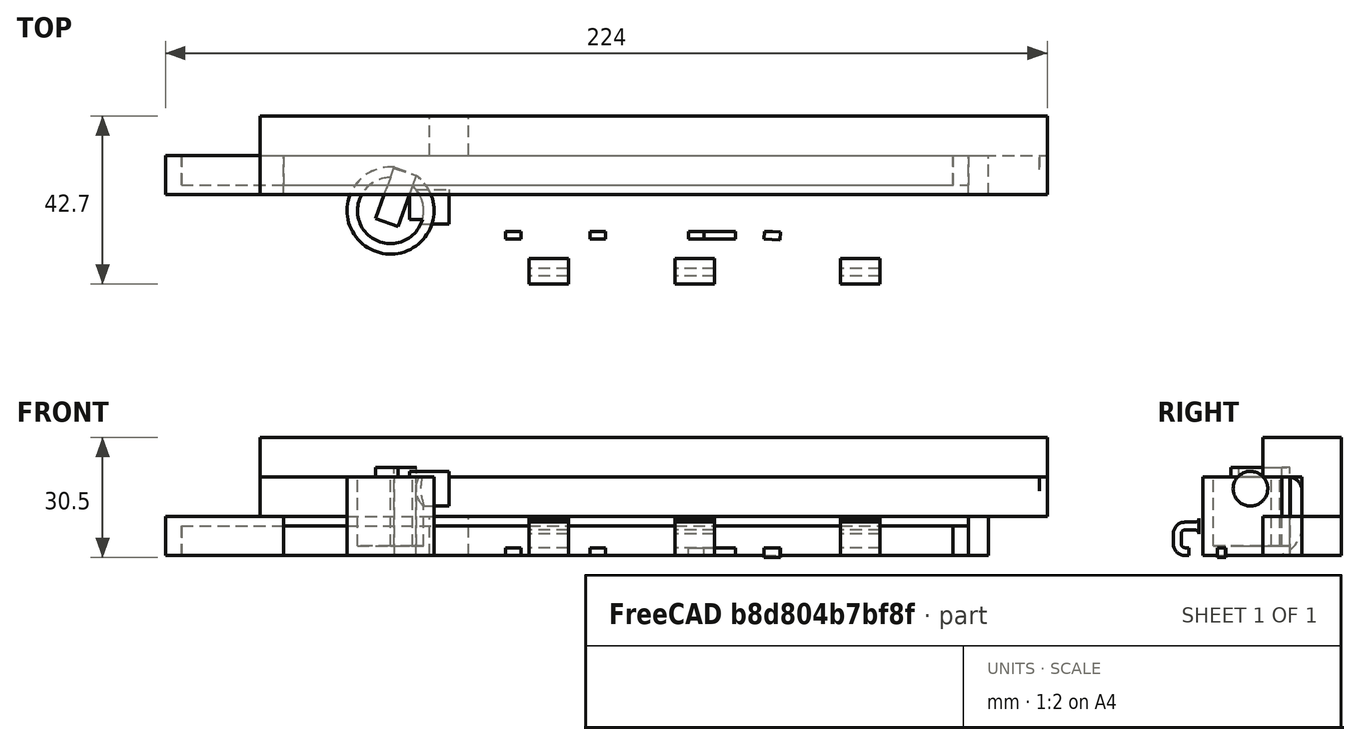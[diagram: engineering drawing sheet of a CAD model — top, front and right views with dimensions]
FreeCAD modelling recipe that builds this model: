
FCSTD DOCUMENT  (FreeCAD 0.19R0.19.2)
Label: v0_72
License: All rights reserved
LicenseURL: http://en.wikipedia.org/wiki/All_rights_reserved
objects: Part::Box×62, Part::Fillet×31, Part::MultiFuse×25, Part::Cut×13, Sketcher::SketchObject×11, Part::Extrusion×9, Part::Cylinder×6, App::MeasureDistance×5, Part::Revolution×1
note: 158 computed .brp shape members not serialized (recipe doc carries the construction recipe); baked Part::Feature solids carry a one-line shape summary decoded from their .brp

FEATURE [Sketcher::SketchObject] Sketch001
  FullyConstrained = true
  sketch-geometry (47):
    g0: Circle CenterX=-129.5 CenterY=-8 CenterZ=0 NormalX=0 NormalY=0 NormalZ=1 AngleXU=0 Radius=1
    g1: Circle CenterX=-129.5 CenterY=-3 CenterZ=0 NormalX=0 NormalY=0 NormalZ=1 AngleXU=0 Radius=1
    g2: Circle CenterX=-124.5 CenterY=-3 CenterZ=0 NormalX=0 NormalY=0 NormalZ=1 AngleXU=0 Radius=1
    g3: BSplineCurve PolesCount=3 KnotsCount=2 Degree=2 IsPeriodic=0
    g4: GeomPoint X=-129.5 Y=-8 Z=0
    g5: GeomPoint X=-124.5 Y=-3 Z=0
    g6: LineSegment StartX=18.6 StartY=-2.9 StartZ=0 EndX=23.6 EndY=-2.9 EndZ=0
    g7: ArcOfCircle CenterX=23.8 CenterY=-14.35 CenterZ=0 NormalX=0 NormalY=0 NormalZ=1 AngleXU=0 Radius=2.3 StartAngle=8e-16 EndAngle=1.5708
    g8: ArcOfCircle CenterX=23.8 CenterY=-18.1 CenterZ=0 NormalX=0 NormalY=0 NormalZ=1 AngleXU=0 Radius=2.3 StartAngle=4.71239 EndAngle=6.28319
    g9: LineSegment StartX=23.8 StartY=-20.4 StartZ=0 EndX=21.1 EndY=-20.4 EndZ=0
    g10: LineSegment StartX=21.1 StartY=-22.9 StartZ=0 EndX=21.1 EndY=-20.4 EndZ=0
    g11: LineSegment StartX=26.1 StartY=-14.35 StartZ=0 EndX=26.1 EndY=-18.1 EndZ=0
    g12: LineSegment StartX=18.6 StartY=-5.40742 StartZ=0 EndX=18.6 EndY=-2.9 EndZ=0
    g13: ArcOfCircle CenterX=18.8 CenterY=-8.1 CenterZ=0 NormalX=0 NormalY=0 NormalZ=1 AngleXU=0 Radius=2.7 StartAngle=1.64494 EndAngle=3.14159
    g14: ArcOfCircle CenterX=18.8 CenterY=-11.85 CenterZ=0 NormalX=0 NormalY=0 NormalZ=1 AngleXU=0 Radius=2.7 StartAngle=3.14159 EndAngle=4.71239
    g15: LineSegment StartX=16.1 StartY=-8.1 StartZ=0 EndX=16.1 EndY=-11.85 EndZ=0
    g16: LineSegment StartX=18.8 StartY=-14.55 StartZ=0 EndX=21.5 EndY=-14.55 EndZ=0
    g17: LineSegment StartX=21.5 StartY=-12.05 StartZ=0 EndX=21.5 EndY=-14.55 EndZ=0
    g18: LineSegment StartX=21.5 StartY=-12.05 StartZ=0 EndX=23.8 EndY=-12.05 EndZ=0
    g19: LineSegment StartX=16.1 StartY=-22.9 StartZ=0 EndX=21.1 EndY=-22.9 EndZ=0
    g20: LineSegment StartX=23.6 StartY=-2.9 StartZ=0 EndX=23.6 EndY=0 EndZ=0
    g21: LineSegment StartX=16.1 StartY=-22.9 StartZ=0 EndX=16.1 EndY=-26.2 EndZ=0
    g22: BSplineCurve PolesCount=3 KnotsCount=2 Degree=2 IsPeriodic=0
    g23: LineSegment StartX=2.6 StartY=-3 StartZ=0 EndX=-124.5 EndY=-3 EndZ=0
    g24: ArcOfCircle CenterX=-134.9 CenterY=-8.6 CenterZ=0 NormalX=0 NormalY=0 NormalZ=1 AngleXU=0 Radius=0.5 StartAngle=4.71238 EndAngle=6.28319
    g25: LineSegment StartX=-141.9 StartY=-9.1 StartZ=0 EndX=-134.9 EndY=-9.1 EndZ=0
    g26: LineSegment StartX=-141.9 StartY=-33.8 StartZ=0 EndX=-141.5 EndY=-33.8 EndZ=0
    g27: LineSegment StartX=-141.9 StartY=-9.1 StartZ=0 EndX=-141.9 EndY=-33.8 EndZ=0
    g28: LineSegment StartX=-134.4 StartY=-8.6 StartZ=0 EndX=-134.4 EndY=0 EndZ=0
    g29: LineSegment StartX=-134.4 StartY=0 StartZ=0 EndX=23.6 EndY=0 EndZ=0
    g30: LineSegment StartX=-133.5 StartY=-26.2 StartZ=0 EndX=16.1 EndY=-26.2 EndZ=0
    g31-g36: Circle x6 (B-spline internal-alignment scaffolding for g37; pole/knot coordinates omitted)
    g37: BSplineCurve PolesCount=6 KnotsCount=4 Degree=3 IsPeriodic=0
    g38-g41: GeomPoint x4 (B-spline internal-alignment scaffolding for g37; pole/knot coordinates omitted)
    g42: BSplineCurve PolesCount=3 KnotsCount=2 Degree=2 IsPeriodic=0
    g43: LineSegment StartX=-129.5 StartY=-8 StartZ=0 EndX=-129.5 EndY=-18.2 EndZ=0
    g44: BSplineCurve PolesCount=3 KnotsCount=2 Degree=2 IsPeriodic=0
    g45: LineSegment StartX=7.6 StartY=-8 StartZ=0 EndX=7.6 EndY=-18.2 EndZ=0
    g46: LineSegment StartX=2.6 StartY=-23.2 StartZ=0 EndX=-124.5 EndY=-23.2 EndZ=0
  constraints (87):
    c: Weight(g0) = 1
    c: Equal(g0,g1)
    c: Equal(g0,g2)
    c: InternalAlignment(g0,g3)
    c: InternalAlignment(g1,g3)
    c: InternalAlignment(g2,g3)
    c: InternalAlignment(g4,g3)
    c: InternalAlignment(g5,g3)
    c: Block(g3)
    c: Block(g8)
    c: Block(g7)
    c: Coincident(g9,g8)
    c: Horizontal(g9)
    c: Vertical(g10)
    c: Coincident(g10,g9)
    c: Coincident(g11,g7)
    c: Coincident(g11,g8)
    c: Vertical(g11)
    c: Vertical(g12)
    c: Block(g12)
    c: Coincident(g6,g12)
    c: Horizontal(g6)
    c: Block(g6)
    c: Coincident(g13,g12)
    c: Block(g14)
    c: Vertical(g15)
    c: Block(g15)
    c: Coincident(g16,g14)
    c: Horizontal(g16)
    c: Vertical(g17)
    c: Coincident(g17,g16)
    c: Block(g17)
    c: Coincident(g18,g7)
    c: Horizontal(g18)
    c: Block(g18)
    c: Coincident(g19,g10)
    c: Horizontal(g19)
    c: Block(g19)
    c: Block(g13)
    c: Coincident(g20,g6)
    c: Vertical(g20)
    c: Vertical(g21)
    c: Block(g21)
    c: Block(g22)
    c: Coincident(g23,g22)
    c: Coincident(g23,g3)
    c: Horizontal(g23)
    c: Block(g24)
    c: Coincident(g25,g24)
    c: Horizontal(g25)
    c: Horizontal(g26)
    c: Block(g26)
    c: Coincident(g27,g25)
    c: Coincident(g27,g26)
    c: Vertical(g27)
    c: Coincident(g28,g24)
    c: Vertical(g28)
    c: Coincident(g29,g28)
    c: Coincident(g29,g20)
    c: Horizontal(g29)
    c: Block(g29)
    c: Block(g25)
    c: Block(g28)
    c: Block(g27)
    c: Coincident(g30,g21)
    c: Horizontal(g30)
    c: Block(g30)
    c: Coincident(g37,g26)
    c: Weight(g31) = 1
    c: Equal(g31, g32-g36) x5
    c: Coincident(g37,g30)
    c: InternalAlignment(g31-g36 -> g37) x6
    c: InternalAlignment(g38-g41 -> g37) x4
    c: Block(g37)
    c: Block(g42)
    c: Coincident(g43,g3)
    c: Coincident(g43,g42)
    c: Vertical(g43)
    c: Distance(g43) = 10.2
    c: Block(g44)
    c: Coincident(g45,g22)
    c: Coincident(g45,g44)
    c: Vertical(g45)
    c: Distance(g45) = 10.2
    c: Coincident(g46,g44)
    c: Coincident(g46,g42)
    c: Horizontal(g46)
FEATURE [Part::Extrusion] Extrude001
  Base = -> Sketch001
  Dir = (0,0,1)
  DirMode = 2
  FaceMakerClass = Part::FaceMakerBullseye
  LengthFwd = 20
  LengthRev = 0
  Solid = true
  Symmetric = false
FEATURE [Sketcher::SketchObject] Sketch004
  FullyConstrained = true
  Placement = pos=(0,0,0) rot=(1,0,0;1.5708rad)
  sketch-geometry (12):
    g0: LineSegment StartX=15.75 StartY=2.5 StartZ=0 EndX=15.75 EndY=0 EndZ=0
    g1: Circle CenterX=15.75 CenterY=2.5 CenterZ=0 NormalX=0 NormalY=0 NormalZ=1 AngleXU=0 Radius=1
    g2: Circle CenterX=10.55 CenterY=2.5 CenterZ=0 NormalX=0 NormalY=0 NormalZ=1 AngleXU=0 Radius=1
    g3: Circle CenterX=10.55 CenterY=8 CenterZ=0 NormalX=0 NormalY=0 NormalZ=1 AngleXU=0 Radius=1
    g4: BSplineCurve PolesCount=3 KnotsCount=2 Degree=2 IsPeriodic=0
    g5: GeomPoint X=15.75 Y=2.5 Z=0
    g6: GeomPoint X=10.55 Y=8 Z=0
    g7: LineSegment StartX=1.9 StartY=8 StartZ=0 EndX=10.55 EndY=8 EndZ=0
    g8: LineSegment StartX=1.9 StartY=-2.4 StartZ=0 EndX=1.9 EndY=8 EndZ=0
    g9: LineSegment StartX=3.30092 StartY=-2.4 StartZ=0 EndX=3.30092 EndY=0 EndZ=0
    g10: LineSegment StartX=15.75 StartY=0 StartZ=0 EndX=3.30092 EndY=0 EndZ=0
    g11: LineSegment StartX=3.30092 StartY=-2.4 StartZ=0 EndX=1.9 EndY=-2.4 EndZ=0
  constraints (26):
    c: Vertical(g0)
    c: Distance(g0) = 2.5
    c: Coincident(g4,g0)
    c: Weight(g1) = 1
    c: Equal(g1,g2)
    c: Equal(g1,g3)
    c: InternalAlignment(g1,g4)
    c: InternalAlignment(g2,g4)
    c: InternalAlignment(g3,g4)
    c: InternalAlignment(g5,g4)
    c: InternalAlignment(g6,g4)
    c: Block(g4)
    c: Coincident(g7,g4)
    c: Horizontal(g7)
    c: Vertical(g8)
    c: Coincident(g8,g7)
    c: Block(g8)
    c: Vertical(g9)
    c: Coincident(g10,g0)
    c: PointOnObject(g10,g-1)
    c: Horizontal(g10)
    c: Coincident(g10,g9)
    c: Block(g9)
    c: Coincident(g11,g9)
    c: Coincident(g11,g8)
    c: Horizontal(g11)
FEATURE [Part::Revolution] Revolve  label="mainScrewStandRevolve"
  Angle = 360
  Axis = (0,0,1)
  Base = (0,0,0)
  FaceMakerClass = Part::FaceMakerBullseye
  Placement = pos=(-101.95,-15.3,0) rot=(0,0,1;0rad)
  Solid = true
  Source = -> Sketch004
  Symmetric = false
FEATURE [Sketcher::SketchObject] Sketch044
  FullyConstrained = true
  MapMode = 4
  Placement = pos=(0,0,0) rot=(0.57735,0.57735,0.57735;2.0944rad)
  sketch-geometry (14):
    g0: LineSegment StartX=6.08745 StartY=-4.11588 StartZ=0 EndX=6.08745 EndY=-2.11589 EndZ=0
    g1: LineSegment StartX=8.08745 StartY=1.38411 StartZ=0 EndX=8.08745 EndY=-1.11589 EndZ=0
    g2: ArcOfCircle CenterX=7.08745 CenterY=-1.11589 CenterZ=0 NormalX=0 NormalY=0 NormalZ=1 AngleXU=0 Radius=1 StartAngle=4.71239 EndAngle=6.28319
    g3: LineSegment StartX=6.08745 StartY=-2.11589 StartZ=0 EndX=7.08745 EndY=-2.11589 EndZ=0
    g4: LineSegment StartX=6.08745 StartY=-4.11588 StartZ=0 EndX=7.08745 EndY=-4.11588 EndZ=0
    g5: ArcOfCircle CenterX=7.08745 CenterY=-1.11589 CenterZ=0 NormalX=0 NormalY=0 NormalZ=1 AngleXU=0 Radius=3 StartAngle=4.71239 EndAngle=6.28319
    g6: ArcOfCircle CenterX=7.08745 CenterY=1.38411 CenterZ=0 NormalX=0 NormalY=0 NormalZ=1 AngleXU=0 Radius=1 StartAngle=5.35e-14 EndAngle=1.5708
    g7: LineSegment StartX=10.0875 StartY=-1.11588 StartZ=0 EndX=10.0875 EndY=1.38411 EndZ=0
    g8: ArcOfCircle CenterX=7.08745 CenterY=1.38411 CenterZ=0 NormalX=0 NormalY=0 NormalZ=1 AngleXU=0 Radius=3 StartAngle=3.57e-14 EndAngle=1.5708
    g9: ArcOfCircle CenterX=4.58745 CenterY=1.38412 CenterZ=0 NormalX=0 NormalY=0 NormalZ=1 AngleXU=0 Radius=1 StartAngle=1.57081 EndAngle=3.14159
    g10: LineSegment StartX=4.58744 StartY=2.38411 StartZ=0 EndX=7.08745 EndY=2.38411 EndZ=0
    g11: LineSegment StartX=4.58745 StartY=4.38411 StartZ=0 EndX=7.08745 EndY=4.38411 EndZ=0
    g12: ArcOfCircle CenterX=4.58745 CenterY=5.38411 CenterZ=0 NormalX=0 NormalY=0 NormalZ=1 AngleXU=0 Radius=1 StartAngle=3.14159 EndAngle=4.71239
    g13: LineSegment StartX=3.58745 StartY=5.38411 StartZ=0 EndX=3.58745 EndY=1.38411 EndZ=0
  constraints (33):
    c: Vertical(g0)
    c: Block(g0)
    c: Block(g1)
    c: Coincident(g2,g1)
    c: Coincident(g3,g0)
    c: Coincident(g3,g2)
    c: Horizontal(g3)
    c: Block(g2)
    c: Coincident(g4,g0)
    c: Horizontal(g4)
    c: Coincident(g5,g2)
    c: Block(g5)
    c: Block(g4)
    c: Coincident(g6,g1)
    c: Block(g6)
    c: Coincident(g7,g5)
    c: Vertical(g7)
    c: Coincident(g8,g6)
    c: Block(g8)
    c: Block(g7)
    c: Coincident(g10,g9)
    c: Coincident(g10,g6)
    c: Horizontal(g10)
    c: Block(g10)
    c: Block(g9)
    c: Coincident(g11,g8)
    c: Horizontal(g11)
    c: Block(g12)
    c: Block(g11)
    c: Coincident(g13,g12)
    c: Coincident(g13,g9)
    c: Vertical(g13)
    c: Tangent(g13,g9)
FEATURE [Sketcher::SketchObject] Sketch045
  FullyConstrained = true
  MapMode = 4
  Placement = pos=(0,0,0) rot=(0.57735,0.57735,0.57735;2.0944rad)
  sketch-geometry (14):
    g0: LineSegment StartX=6.08745 StartY=-4.11588 StartZ=0 EndX=6.08745 EndY=-2.11589 EndZ=0
    g1: LineSegment StartX=8.08745 StartY=1.38411 StartZ=0 EndX=8.08745 EndY=-1.11589 EndZ=0
    g2: ArcOfCircle CenterX=7.08745 CenterY=-1.11589 CenterZ=0 NormalX=0 NormalY=0 NormalZ=1 AngleXU=0 Radius=1 StartAngle=4.71239 EndAngle=6.28319
    g3: LineSegment StartX=6.08745 StartY=-2.11589 StartZ=0 EndX=7.08745 EndY=-2.11589 EndZ=0
    g4: LineSegment StartX=6.08745 StartY=-4.11588 StartZ=0 EndX=7.08745 EndY=-4.11588 EndZ=0
    g5: ArcOfCircle CenterX=7.08745 CenterY=-1.11589 CenterZ=0 NormalX=0 NormalY=0 NormalZ=1 AngleXU=0 Radius=3 StartAngle=4.71239 EndAngle=6.28319
    g6: ArcOfCircle CenterX=7.08745 CenterY=1.38411 CenterZ=0 NormalX=0 NormalY=0 NormalZ=1 AngleXU=0 Radius=1 StartAngle=5.35e-14 EndAngle=1.5708
    g7: LineSegment StartX=10.0875 StartY=-1.11588 StartZ=0 EndX=10.0875 EndY=1.38411 EndZ=0
    g8: ArcOfCircle CenterX=7.08745 CenterY=1.38411 CenterZ=0 NormalX=0 NormalY=0 NormalZ=1 AngleXU=0 Radius=3 StartAngle=3.57e-14 EndAngle=1.5708
    g9: ArcOfCircle CenterX=4.58745 CenterY=1.38412 CenterZ=0 NormalX=0 NormalY=0 NormalZ=1 AngleXU=0 Radius=1 StartAngle=1.57081 EndAngle=3.14159
    g10: LineSegment StartX=4.58744 StartY=2.38411 StartZ=0 EndX=7.08745 EndY=2.38411 EndZ=0
    g11: LineSegment StartX=4.58745 StartY=4.38411 StartZ=0 EndX=7.08745 EndY=4.38411 EndZ=0
    g12: ArcOfCircle CenterX=4.58745 CenterY=5.38411 CenterZ=0 NormalX=0 NormalY=0 NormalZ=1 AngleXU=0 Radius=1 StartAngle=3.14159 EndAngle=4.71239
    g13: LineSegment StartX=3.58745 StartY=5.38411 StartZ=0 EndX=3.58745 EndY=1.38411 EndZ=0
  constraints (33):
    c: Vertical(g0)
    c: Block(g0)
    c: Block(g1)
    c: Coincident(g2,g1)
    c: Coincident(g3,g0)
    c: Coincident(g3,g2)
    c: Horizontal(g3)
    c: Block(g2)
    c: Coincident(g4,g0)
    c: Horizontal(g4)
    c: Coincident(g5,g2)
    c: Block(g5)
    c: Block(g4)
    c: Coincident(g6,g1)
    c: Block(g6)
    c: Coincident(g7,g5)
    c: Vertical(g7)
    c: Coincident(g8,g6)
    c: Block(g8)
    c: Block(g7)
    c: Coincident(g10,g9)
    c: Coincident(g10,g6)
    c: Horizontal(g10)
    c: Block(g10)
    c: Block(g9)
    c: Coincident(g11,g8)
    c: Horizontal(g11)
    c: Block(g12)
    c: Block(g11)
    c: Coincident(g13,g12)
    c: Coincident(g13,g9)
    c: Vertical(g13)
    c: Tangent(g13,g9)
FEATURE [Part::Extrusion] Extrude040
  Base = -> Sketch045
  Dir = (1,0,0)
  DirMode = 2
  FaceMakerClass = Part::FaceMakerBullseye
  LengthFwd = 10
  LengthRev = 0
  Placement = pos=(-71.7,-22.61,4.115) rot=(0,0,1;3.14159rad)
  Solid = true
  Symmetric = false
FEATURE [Part::Box] Box017  label="Cube017"
  AttacherType = Attacher::AttachEngine3D
  Height = 2
  Length = 2
  Placement = pos=(-85.7,-21.3,0) rot=(0,0,1;0rad)
  Width = 2
FEATURE [Part::Box] Box018  label="Cube018"
  AttacherType = Attacher::AttachEngine3D
  Height = 2
  Length = 2
  Placement = pos=(-87.7,-21.3,0) rot=(0,0,1;0rad)
  Width = 2
FEATURE [Part::MultiFuse] Fusion
  Shapes = -> [Box017,Box018]
FEATURE [Part::Box] Box021  label="Cube021"
  AttacherType = Attacher::AttachEngine3D
  Height = 2
  Length = 2
  Placement = pos=(-85.7,-21.3,0) rot=(0,0,1;0rad)
  Width = 2
FEATURE [Part::Box] Box022  label="Cube022"
  AttacherType = Attacher::AttachEngine3D
  Height = 2
  Length = 2
  Placement = pos=(-87.7,-21.3,0) rot=(0,0,1;0rad)
  Width = 2
FEATURE [Part::Box] Box023  label="Cube023"
  AttacherType = Attacher::AttachEngine3D
  Height = 2
  Length = 2
  Placement = pos=(-85.7,-21.3,0) rot=(0,0,1;0rad)
  Width = 2
FEATURE [Part::Box] Box024  label="Cube024"
  AttacherType = Attacher::AttachEngine3D
  Height = 2
  Length = 2
  Placement = pos=(-87.7,-21.3,0) rot=(0,0,1;0rad)
  Width = 2
FEATURE [Part::Box] Box026  label="Cube026"
  AttacherType = Attacher::AttachEngine3D
  Height = 2
  Length = 2
  Placement = pos=(-87.7,-21.3,0) rot=(0,0,1;0rad)
  Width = 2
FEATURE [Part::Box] Box  label="Cube"
  AttacherType = Attacher::AttachEngine3D
  Height = 10
  Length = 10
  Placement = pos=(-107,0,0) rot=(0,0,1;0rad)
  Width = 10
FEATURE [Sketcher::SketchObject] Sketch046
  FullyConstrained = true
  MapMode = 4
  Placement = pos=(0,0,0) rot=(0.57735,0.57735,0.57735;2.0944rad)
  sketch-geometry (14):
    g0: LineSegment StartX=6.08745 StartY=-4.11588 StartZ=0 EndX=6.08745 EndY=-2.11589 EndZ=0
    g1: LineSegment StartX=8.08745 StartY=1.38411 StartZ=0 EndX=8.08745 EndY=-1.11589 EndZ=0
    g2: ArcOfCircle CenterX=7.08745 CenterY=-1.11589 CenterZ=0 NormalX=0 NormalY=0 NormalZ=1 AngleXU=0 Radius=1 StartAngle=4.71239 EndAngle=6.28319
    g3: LineSegment StartX=6.08745 StartY=-2.11589 StartZ=0 EndX=7.08745 EndY=-2.11589 EndZ=0
    g4: LineSegment StartX=6.08745 StartY=-4.11588 StartZ=0 EndX=7.08745 EndY=-4.11588 EndZ=0
    g5: ArcOfCircle CenterX=7.08745 CenterY=-1.11589 CenterZ=0 NormalX=0 NormalY=0 NormalZ=1 AngleXU=0 Radius=3 StartAngle=4.71239 EndAngle=6.28319
    g6: ArcOfCircle CenterX=7.08745 CenterY=1.38411 CenterZ=0 NormalX=0 NormalY=0 NormalZ=1 AngleXU=0 Radius=1 StartAngle=5.35e-14 EndAngle=1.5708
    g7: LineSegment StartX=10.0875 StartY=-1.11588 StartZ=0 EndX=10.0875 EndY=1.38411 EndZ=0
    g8: ArcOfCircle CenterX=7.08745 CenterY=1.38411 CenterZ=0 NormalX=0 NormalY=0 NormalZ=1 AngleXU=0 Radius=3 StartAngle=3.57e-14 EndAngle=1.5708
    g9: ArcOfCircle CenterX=4.58745 CenterY=1.38412 CenterZ=0 NormalX=0 NormalY=0 NormalZ=1 AngleXU=0 Radius=1 StartAngle=1.57081 EndAngle=3.14159
    g10: LineSegment StartX=4.58744 StartY=2.38411 StartZ=0 EndX=7.08745 EndY=2.38411 EndZ=0
    g11: LineSegment StartX=4.58745 StartY=4.38411 StartZ=0 EndX=7.08745 EndY=4.38411 EndZ=0
    g12: ArcOfCircle CenterX=4.58745 CenterY=5.38411 CenterZ=0 NormalX=0 NormalY=0 NormalZ=1 AngleXU=0 Radius=1 StartAngle=3.14159 EndAngle=4.71239
    g13: LineSegment StartX=3.58745 StartY=5.38411 StartZ=0 EndX=3.58745 EndY=1.38411 EndZ=0
  constraints (33):
    c: Vertical(g0)
    c: Block(g0)
    c: Block(g1)
    c: Coincident(g2,g1)
    c: Coincident(g3,g0)
    c: Coincident(g3,g2)
    c: Horizontal(g3)
    c: Block(g2)
    c: Coincident(g4,g0)
    c: Horizontal(g4)
    c: Coincident(g5,g2)
    c: Block(g5)
    c: Block(g4)
    c: Coincident(g6,g1)
    c: Block(g6)
    c: Coincident(g7,g5)
    c: Vertical(g7)
    c: Coincident(g8,g6)
    c: Block(g8)
    c: Block(g7)
    c: Coincident(g10,g9)
    c: Coincident(g10,g6)
    c: Horizontal(g10)
    c: Block(g10)
    c: Block(g9)
    c: Coincident(g11,g8)
    c: Horizontal(g11)
    c: Block(g12)
    c: Block(g11)
    c: Coincident(g13,g12)
    c: Coincident(g13,g9)
    c: Vertical(g13)
    c: Tangent(g13,g9)
FEATURE [Part::Extrusion] Extrude041
  Base = -> Sketch046
  Dir = (1,0,0)
  DirMode = 2
  FaceMakerClass = Part::FaceMakerBullseye
  LengthFwd = 10
  LengthRev = 0
  Placement = pos=(7.5,-22.61,4.115) rot=(0,0,1;3.14159rad)
  Solid = true
  Symmetric = false
FEATURE [Part::Box] Box027  label="Cube027"
  AttacherType = Attacher::AttachEngine3D
  Height = 2
  Length = 2
  Placement = pos=(-85.7,-21.3,0) rot=(0,0,1;0rad)
  Width = 2
FEATURE [Part::Box] Box028  label="Cube028"
  AttacherType = Attacher::AttachEngine3D
  Height = 2
  Length = 2
  Placement = pos=(-87.7,-21.3,0) rot=(0,0,1;0rad)
  Width = 2
FEATURE [Part::MultiFuse] Fusion009
  Placement = pos=(21.5,0,0) rot=(0,0,1;0rad)
  Shapes = -> [Box027,Box028]
FEATURE [Part::Box] Box029  label="Cube029"
  AttacherType = Attacher::AttachEngine3D
  Height = 2
  Length = 2
  Placement = pos=(-87.7,-21.3,0) rot=(0,0,1;0rad)
  Width = 2
FEATURE [Part::Box] Box030  label="Cube030"
  AttacherType = Attacher::AttachEngine3D
  Height = 2
  Length = 2
  Placement = pos=(-85.7,-21.3,0) rot=(0,0,1;0rad)
  Width = 2
FEATURE [Part::MultiFuse] Fusion010
  Shapes = -> [Box030,Box029]
FEATURE [Part::Box] Box032  label="Cube032"
  AttacherType = Attacher::AttachEngine3D
  Height = 2
  Length = 2
  Placement = pos=(-85.7,-21.3,0) rot=(0,0,1;0rad)
  Width = 2
FEATURE [Part::Box] Box033  label="Cube033"
  AttacherType = Attacher::AttachEngine3D
  Height = 2
  Length = 2
  Placement = pos=(-87.7,-21.3,0) rot=(0,0,1;0rad)
  Width = 2
FEATURE [Part::MultiFuse] Fusion011
  Shapes = -> [Box032,Box033]
FEATURE [Part::Box] Box034  label="Cube034"
  AttacherType = Attacher::AttachEngine3D
  Height = 2
  Length = 2
  Placement = pos=(-85.7,-21.3,0) rot=(0,0,1;0rad)
  Width = 2
FEATURE [Part::Box] Box035  label="Cube035"
  AttacherType = Attacher::AttachEngine3D
  Height = 2
  Length = 2
  Placement = pos=(-87.7,-21.3,0) rot=(0,0,1;0rad)
  Width = 2
FEATURE [Part::Box] Box036  label="Cube036"
  AttacherType = Attacher::AttachEngine3D
  Height = 2
  Length = 2
  Placement = pos=(-85.7,-21.3,0) rot=(0,0,1;0rad)
  Width = 2
FEATURE [Part::Box] Box037  label="Cube037"
  AttacherType = Attacher::AttachEngine3D
  Height = 2
  Length = 2
  Placement = pos=(-87.7,-21.3,0) rot=(0,0,1;0rad)
  Width = 2
FEATURE [Part::Box] Box038  label="Cube038"
  AttacherType = Attacher::AttachEngine3D
  Height = 2
  Length = 2
  Placement = pos=(-85.7,-21.3,0) rot=(0,0,1;0rad)
  Width = 2
FEATURE [Part::Box] Box039  label="Cube039"
  AttacherType = Attacher::AttachEngine3D
  Height = 2
  Length = 2
  Placement = pos=(-87.7,-21.3,0) rot=(0,0,1;0rad)
  Width = 2
FEATURE [Part::Box] Box040  label="Cube040"
  AttacherType = Attacher::AttachEngine3D
  Height = 2
  Length = 2
  Placement = pos=(-85.7,-21.3,0) rot=(0,0,1;0rad)
  Width = 2
FEATURE [Part::Box] Box041  label="Cube041"
  AttacherType = Attacher::AttachEngine3D
  Height = 2
  Length = 2
  Placement = pos=(-87.7,-21.3,0) rot=(0,0,1;0rad)
  Width = 2
FEATURE [Part::Box] Box042  label="Cube042"
  AttacherType = Attacher::AttachEngine3D
  Height = 2
  Length = 2
  Placement = pos=(-87.7,-21.3,0) rot=(0,0,1;0rad)
  Width = 2
FEATURE [Part::Box] Box043  label="Cube043"
  AttacherType = Attacher::AttachEngine3D
  Height = 2
  Length = 2
  Placement = pos=(-85.7,-21.3,0) rot=(0,0,1;0rad)
  Width = 2
FEATURE [Part::MultiFuse] Fusion019
  Placement = pos=(46.5,0,0) rot=(0,0,1;0rad)
  Shapes = -> [Box043,Box042]
FEATURE [Part::Box] Box044  label="Cube044"
  AttacherType = Attacher::AttachEngine3D
  Height = 2
  Length = 2
  Placement = pos=(-87.7,-21.3,0) rot=(0,0,1;0rad)
  Width = 2
FEATURE [Part::Box] Box045  label="Cube045"
  AttacherType = Attacher::AttachEngine3D
  Height = 2
  Length = 2
  Placement = pos=(-85.7,-21.3,0) rot=(0,0,1;0rad)
  Width = 2
FEATURE [Part::MultiFuse] Fusion020
  Placement = pos=(69.3,0,0) rot=(0,0,1;0rad)
  Shapes = -> [Box045,Box044]
FEATURE [Part::Box] Box046  label="Cube046"
  AttacherType = Attacher::AttachEngine3D
  Height = 2
  Length = 2
  Placement = pos=(-87.7,-21.3,0) rot=(0,0,1;0rad)
  Width = 2
FEATURE [Part::Box] Box047  label="Cube047"
  AttacherType = Attacher::AttachEngine3D
  Height = 2
  Length = 2
  Placement = pos=(-85.7,-21.3,0) rot=(0,0,1;0rad)
  Width = 2
FEATURE [Part::MultiFuse] Fusion021
  Placement = pos=(73.3,0,0) rot=(0,0,1;0rad)
  Shapes = -> [Box047,Box046]
FEATURE [Part::Box] Box048  label="Cube048"
  AttacherType = Attacher::AttachEngine3D
  Height = 2
  Length = 2
  Placement = pos=(-87.7,-21.3,0) rot=(0,0,1;0rad)
  Width = 2
FEATURE [Part::Box] Box049  label="Cube049"
  AttacherType = Attacher::AttachEngine3D
  Height = 2
  Length = 2
  Placement = pos=(-85.7,-21.3,0) rot=(0,0,1;0rad)
  Width = 2
FEATURE [Part::MultiFuse] Fusion022
  Placement = pos=(64.3,0,0) rot=(0,0,1;0rad)
  Shapes = -> [Box049,Box048]
FEATURE [Part::MultiFuse] Fusion024
  Shapes = -> [Box034,Box035,Box036,Box037,Box038,Box039,Box040,Box041]
FEATURE [Part::MultiFuse] Fusion025
  Shapes = -> [Box021,Box022,Box023,Box024,Box026]
FEATURE [Part::Box] Box005  label="Cube005"
  AttacherType = Attacher::AttachEngine3D
  Height = 10
  Length = 198
  Placement = pos=(-30,0,0) rot=(0,0,1;0rad)
  Width = 10
FEATURE [Part::Box] Box004  label="Cube004"
  AttacherType = Attacher::AttachEngine3D
  Height = 10
  Length = 200
  Placement = pos=(-30,0,0) rot=(0,0,1;0rad)
  Width = 10
FEATURE [Part::Fillet] Fillet020
  Base = -> Box004
  Edges = 1 edges r=3.6: [Edge12]
FEATURE [Sketcher::SketchObject] Sketch
  FullyConstrained = true
  sketch-geometry (35):
    g0: Circle CenterX=-101.95 CenterY=-14.3 CenterZ=0 NormalX=0 NormalY=0 NormalZ=1 AngleXU=0 Radius=3.25
    g1: LineSegment StartX=16.1 StartY=-26.2 StartZ=0 EndX=16.1 EndY=-22.9 EndZ=0
    g2: ArcOfCircle CenterX=23.8 CenterY=-14.35 CenterZ=0 NormalX=0 NormalY=0 NormalZ=1 AngleXU=0 Radius=2.3 StartAngle=8e-16 EndAngle=1.5708
    g3: LineSegment StartX=18.6 StartY=-5.40742 StartZ=0 EndX=18.6 EndY=-2.9 EndZ=0
    g4: LineSegment StartX=18.6 StartY=-2.9 StartZ=0 EndX=23.6 EndY=-2.9 EndZ=0
    g5: LineSegment StartX=23.6 StartY=-2.9 StartZ=0 EndX=23.6 EndY=2.58e-14 EndZ=0
    g6: LineSegment StartX=18.8 StartY=-14.55 StartZ=0 EndX=21.5 EndY=-14.55 EndZ=0
    g7: LineSegment StartX=21.5 StartY=-12.05 StartZ=0 EndX=21.5 EndY=-14.55 EndZ=0
    g8: LineSegment StartX=21.5 StartY=-12.05 StartZ=0 EndX=23.8 EndY=-12.05 EndZ=0
    g9: ArcOfCircle CenterX=23.8 CenterY=-18.1 CenterZ=0 NormalX=0 NormalY=0 NormalZ=1 AngleXU=0 Radius=2.3 StartAngle=4.71239 EndAngle=6.28319
    g10: LineSegment StartX=23.8 StartY=-20.4 StartZ=0 EndX=21.1 EndY=-20.4 EndZ=0
    g11: LineSegment StartX=26.1 StartY=-14.35 StartZ=0 EndX=26.1 EndY=-18.1 EndZ=0
    g12: ArcOfCircle CenterX=18.8 CenterY=-8.1 CenterZ=0 NormalX=0 NormalY=0 NormalZ=1 AngleXU=0 Radius=2.7 StartAngle=1.64494 EndAngle=3.14159
    g13: ArcOfCircle CenterX=18.8 CenterY=-11.85 CenterZ=0 NormalX=0 NormalY=0 NormalZ=1 AngleXU=0 Radius=2.7 StartAngle=3.14159 EndAngle=4.71239
    g14: LineSegment StartX=16.1 StartY=-8.1 StartZ=0 EndX=16.1 EndY=-11.85 EndZ=0
    g15: LineSegment StartX=21.1 StartY=-22.9 StartZ=0 EndX=21.1 EndY=-20.4 EndZ=0
    g16: LineSegment StartX=16.1 StartY=-22.9 StartZ=0 EndX=21.1 EndY=-22.9 EndZ=0
    g17: LineSegment StartX=23.6 StartY=2.58e-14 StartZ=0 EndX=-134.4 EndY=2.58e-14 EndZ=0
    g18: LineSegment StartX=-134.4 StartY=2.59e-14 StartZ=0 EndX=-134.4 EndY=-8.6 EndZ=0
    g19: ArcOfCircle CenterX=-134.9 CenterY=-8.6 CenterZ=0 NormalX=0 NormalY=0 NormalZ=1 AngleXU=0 Radius=0.5 StartAngle=4.71238 EndAngle=6.28319
    g20: LineSegment StartX=-134.9 StartY=-9.1 StartZ=0 EndX=-141.9 EndY=-9.1 EndZ=0
    g21: LineSegment StartX=-141.9 StartY=-9.1 StartZ=0 EndX=-141.9 EndY=-33.8 EndZ=0
    g22: LineSegment StartX=-141.9 StartY=-33.8 StartZ=0 EndX=-141.5 EndY=-33.8 EndZ=0
    g23: LineSegment StartX=-133.5 StartY=-26.2 StartZ=0 EndX=16.1 EndY=-26.2 EndZ=0
    g24-g29: Circle x6 (B-spline internal-alignment scaffolding for g30; pole/knot coordinates omitted)
    g30: BSplineCurve PolesCount=6 KnotsCount=4 Degree=3 IsPeriodic=0
    g31-g34: GeomPoint x4 (B-spline internal-alignment scaffolding for g30; pole/knot coordinates omitted)
  constraints (61):
    c: Block(g0)
    c: Vertical(g1)
    c: Distance(g1) = 3.3
    c: Block(g9)
    c: Block(g2)
    c: Coincident(g10,g9)
    c: Horizontal(g10)
    c: Vertical(g15)
    c: Coincident(g15,g10)
    c: Coincident(g11,g2)
    c: Coincident(g11,g9)
    c: Vertical(g11)
    c: Vertical(g3)
    c: Block(g3)
    c: Coincident(g4,g3)
    c: Horizontal(g4)
    c: Vertical(g5)
    c: Block(g5)
    c: Block(g4)
    c: Coincident(g12,g3)
    c: Block(g13)
    c: Coincident(g14,g12)
    c: Vertical(g14)
    c: Block(g14)
    c: Coincident(g6,g13)
    c: Horizontal(g6)
    c: Vertical(g7)
    c: Coincident(g7,g6)
    c: Block(g7)
    c: Coincident(g8,g2)
    c: Horizontal(g8)
    c: Block(g8)
    c: Coincident(g16,g15)
    c: Horizontal(g16)
    c: Block(g16)
    c: Block(g12)
    c: Coincident(g16,g1)
    c: Coincident(g17,g5)
    c: Horizontal(g17)
    c: Vertical(g18)
    c: Horizontal(g20)
    c: Coincident(g19,g18)
    c: Coincident(g19,g20)
    c: Block(g19)
    c: Coincident(g21,g20)
    c: Vertical(g21)
    c: Block(g21)
    c: Coincident(g22,g21)
    c: Horizontal(g22)
    c: Block(g22)
    c: Block(g18)
    c: Coincident(g18,g17)
    c: Coincident(g23,g1)
    c: Horizontal(g23)
    c: Distance(g23) = 149.6
    c: Coincident(g30,g22)
    c: Weight(g24) = 1
    c: Equal(g24, g25-g29) x5
    c: InternalAlignment(g24-g29 -> g30) x6
    c: InternalAlignment(g31-g34 -> g30) x4
    c: Block(g30)
FEATURE [Part::Extrusion] Extrude
  Base = -> Sketch
  Dir = (0,0,1)
  DirMode = 2
  FaceMakerClass = Part::FaceMakerBullseye
  LengthFwd = 2.4
  LengthRev = 0
  Solid = true
  Symmetric = false
FEATURE [Part::Box] Box051  label="Cube051"
  AttacherType = Attacher::AttachEngine3D
  Height = 10
  Length = 198
  Placement = pos=(-30,0,0) rot=(0,0,1;0rad)
  Width = 10
FEATURE [Part::Box] Box052  label="Cube052"
  AttacherType = Attacher::AttachEngine3D
  Height = 5
  Length = 200
  Placement = pos=(-30,6.4,10) rot=(1,0,0;0rad)
  Width = 5
FEATURE [Part::Box] Box053  label="Cube053"
  AttacherType = Attacher::AttachEngine3D
  Height = 5
  Length = 200
  Placement = pos=(-30,6.4,10) rot=(1,0,0;0.872665rad)
  Width = 5
FEATURE [Part::Box] Box054  label="Cube054"
  AttacherType = Attacher::AttachEngine3D
  Height = 10
  Length = 200
  Placement = pos=(-30,0,0) rot=(0,0,1;0rad)
  Width = 10
FEATURE [Part::Fillet] Fillet021
  Base = -> Box054
  Edges = 1 edges r=3.6: [Edge12]
FEATURE [Part::Cut] Cut015
  Base = -> Box051
  Tool = -> Fillet021
FEATURE [Part::MultiFuse] Fusion033  label="removeFromMainFusion014"
  Placement = pos=(-120,-10,10) rot=(0,0,1;0rad)
  Shapes = -> [Box053,Box052,Cut015]
FEATURE [Part::Box] Box055  label="Cube055"
  AttacherType = Attacher::AttachEngine3D
  Height = 10
  Length = 190
  Placement = pos=(-30,0,0) rot=(0,0,1;0rad)
  Width = 10
FEATURE [Part::Box] Box056  label="Cube056"
  AttacherType = Attacher::AttachEngine3D
  Height = 10
  Length = 190
  Placement = pos=(-35,0,0) rot=(0,0,1;0rad)
  Width = 10
FEATURE [Part::Fillet] Fillet022
  Base = -> Box055
  Edges = 1 edges r=7.5: [Edge11]
FEATURE [Part::Cut] Cut014  label="filletMain001"
  Base = -> Box056
  Placement = pos=(-120,-10,0) rot=(0,0,1;0rad)
  Tool = -> Fillet022
FEATURE [Part::MultiFuse] Fusion032  label="removeFromMain001"
  Shapes = -> [Fusion033,Cut014]
FEATURE [Part::Cut] Cut017
  Base = -> Extrude
  Tool = -> Fusion032
FEATURE [Part::Box] Box063  label="Cube063"
  AttacherType = Attacher::AttachEngine3D
  Height = 10
  Length = 198
  Placement = pos=(-30,0,0) rot=(0,0,1;0rad)
  Width = 10
FEATURE [Part::Box] Box064  label="Cube064"
  AttacherType = Attacher::AttachEngine3D
  Height = 5
  Length = 200
  Placement = pos=(-30,6.4,10) rot=(1,0,0;0rad)
  Width = 5
FEATURE [Part::Box] Box065  label="Cube065"
  AttacherType = Attacher::AttachEngine3D
  Height = 5
  Length = 200
  Placement = pos=(-30,6.4,10) rot=(1,0,0;0.872665rad)
  Width = 5
FEATURE [Part::Box] Box066  label="Cube066"
  AttacherType = Attacher::AttachEngine3D
  Height = 10
  Length = 200
  Placement = pos=(-30,0,0) rot=(0,0,1;0rad)
  Width = 10
FEATURE [Part::Fillet] Fillet023
  Base = -> Box066
  Edges = 1 edges r=3.6: [Edge12]
FEATURE [Part::Cut] Cut018
  Base = -> Box063
  Tool = -> Fillet023
FEATURE [Part::MultiFuse] Fusion035  label="removeFromMainFusion015"
  Placement = pos=(-120,-10,10) rot=(0,0,1;0rad)
  Shapes = -> [Box065,Box064,Cut018]
FEATURE [Part::Box] Box067  label="Cube067"
  AttacherType = Attacher::AttachEngine3D
  Height = 10
  Length = 190
  Placement = pos=(-30,0,0) rot=(0,0,1;0rad)
  Width = 10
FEATURE [Part::Fillet] Fillet024
  Base = -> Box067
  Edges = 1 edges r=7.5: [Edge11]
FEATURE [Part::Box] Box068  label="Cube068"
  AttacherType = Attacher::AttachEngine3D
  Height = 10
  Length = 190
  Placement = pos=(-35,0,0) rot=(0,0,1;0rad)
  Width = 10
FEATURE [Part::Cut] Cut019  label="filletMain002"
  Base = -> Box068
  Placement = pos=(-120,-10,0) rot=(0,0,1;0rad)
  Tool = -> Fillet024
FEATURE [Part::MultiFuse] Fusion036  label="removeFromMain002"
  Shapes = -> [Fusion035,Cut019]
FEATURE [Part::Box] Box069  label="Cube069"
  AttacherType = Attacher::AttachEngine3D
  Height = 20
  Length = 10
  Placement = pos=(-144.4,-8,0) rot=(0,0,1;0rad)
  Width = 10
FEATURE [Part::Box] Box070  label="Cube070"
  AttacherType = Attacher::AttachEngine3D
  Height = 20
  Length = 30
  Placement = pos=(-120,0,0) rot=(0,0,1;0rad)
  Width = 20
FEATURE [Part::MultiFuse] Fusion037  label="removeFromIntegrityIncreaserFusion037"
  Shapes = -> [Box069,Box070,Fusion036]
FEATURE [Sketcher::SketchObject] Sketch047
  FullyConstrained = true
  sketch-geometry (4):
    g0: LineSegment StartX=20.5 StartY=-1.82002 StartZ=0 EndX=20.5 EndY=-36 EndZ=0
    g1: LineSegment StartX=32.7 StartY=-36 StartZ=0 EndX=32.7 EndY=-1.82002 EndZ=0
    g2: LineSegment StartX=20.5 StartY=-1.82002 StartZ=0 EndX=32.7 EndY=-1.82002 EndZ=0
    g3: LineSegment StartX=20.5 StartY=-36 StartZ=0 EndX=32.7 EndY=-36 EndZ=0
  constraints (12):
    c: Vertical(g0)
    c: Distance(g0) = 34.18
    c: Vertical(g1)
    c: Block(g0)
    c: Coincident(g2,g0)
    c: Horizontal(g2)
    c: Coincident(g2,g1)
    c: Block(g2)
    c: Block(g1)
    c: Coincident(g3,g0)
    c: Coincident(g3,g1)
    c: Horizontal(g3)
FEATURE [Part::MultiFuse] Fusion038
  Placement = pos=(-18.8,0,0) rot=(0,0,1;0rad)
  Shapes = -> [Fusion020,Fusion021]
FEATURE [Part::Box] Box071  label="Cube071"
  AttacherType = Attacher::AttachEngine3D
  Height = 2
  Length = 2
  Placement = pos=(-87.7,-21.3,0) rot=(0,0,1;0rad)
  Width = 2
FEATURE [Part::Box] Box072  label="Cube072"
  AttacherType = Attacher::AttachEngine3D
  Height = 2
  Length = 2
  Placement = pos=(-85.7,-21.3,0) rot=(0,0,1;0rad)
  Width = 2
FEATURE [Part::MultiFuse] Fusion039
  Placement = pos=(64.3,0,-0.5) rot=(0,0,1;0rad)
  Shapes = -> [Box072,Box071]
FEATURE [Part::MultiFuse] Fusion040  label="removeFromHook"
  Placement = pos=(2.4,-1.09,0) rot=(0,0,-1;0.045379rad)
  Shapes = -> [Fusion022,Fusion039]
FEATURE [Part::Cut] Cut021
  Base = -> Box005
  Tool = -> Fillet020
FEATURE [Part::Box] Box073  label="Cube073"
  AttacherType = Attacher::AttachEngine3D
  Height = 10
  Length = 200
  Placement = pos=(-30,10,0) rot=(0,0,1;0rad)
  Width = 10
FEATURE [Part::Box] Box074  label="Cube074"
  AttacherType = Attacher::AttachEngine3D
  Height = 10
  Length = 200
  Placement = pos=(-30,0,10) rot=(0,0,1;0rad)
  Width = 10
FEATURE [Part::Box] Box075  label="Cube075"
  AttacherType = Attacher::AttachEngine3D
  Height = 10
  Length = 200
  Placement = pos=(-30,10,10) rot=(0,0,1;0rad)
  Width = 10
FEATURE [Part::MultiFuse] Fusion043  label="removeFromMainFusion043"
  Placement = pos=(-120,-10,10) rot=(0,0,1;0rad)
  Shapes = -> [Cut021,Box074,Box073,Box075]
FEATURE [Part::Box] Box076  label="Cube076"
  AttacherType = Attacher::AttachEngine3D
  Height = 10
  Length = 200
  Placement = pos=(-160,0,0) rot=(0,0,1;0rad)
  Width = 10
FEATURE [Part::Box] Box077  label="Cube077"
  AttacherType = Attacher::AttachEngine3D
  Height = 10
  Length = 170
  Placement = pos=(-130,0,0) rot=(0,0,1;0rad)
  Width = 10
FEATURE [Part::Fillet] Fillet028
  Base = -> Box077
  Edges = 1 edges r=7.5: [Edge11]
FEATURE [Part::Cut] Cut024
  Base = -> Box076
  Placement = pos=(-14,-10,0) rot=(0,0,1;0rad)
  Tool = -> Fillet028
FEATURE [Part::Box] Box078  label="Cube078"
  AttacherType = Attacher::AttachEngine3D
  Height = 10
  Length = 200
  Width = 10
FEATURE [Part::Box] Box079  label="Cube079"
  AttacherType = Attacher::AttachEngine3D
  Height = 10
  Length = 205
  Placement = pos=(10,0,0) rot=(0,0,1;0rad)
  Width = 10
FEATURE [Part::Fillet] Fillet029
  Base = -> Box078
  Edges = 1 edges r=7.5: [Edge11]
  Placement = pos=(10,0,0) rot=(0,0,1;0rad)
FEATURE [Part::Cut] Cut025  label="removeFromMainCut025"
  Base = -> Box079
  Placement = pos=(-180,-10,0) rot=(0,0,1;0rad)
  Tool = -> Fillet029
FEATURE [Part::Cylinder] Cylinder001
  Angle = 360
  AttacherType = Attacher::AttachEngine3D
  Height = 10
  Placement = pos=(-36.2,-2,12) rot=(0,1,0;1.5708rad)
  Radius = 2
FEATURE [App::MeasureDistance] Distance  label="Distance: 4.02 mm"
  Distance = 4.02
  P1 = (-33.21,5.8978,9.90268)
  P2 = (-29.19,5.8978,9.90268)
FEATURE [Part::Fillet] Fillet030
  Base = -> Cylinder001
  Edges = 1 edges r=1.8: [Edge3]
FEATURE [Part::Fillet] Fillet031
  Base = -> Fillet030
  Edges = 1 edges r=1.8: [Edge2]
FEATURE [Part::Cylinder] Cylinder003
  Angle = 360
  AttacherType = Attacher::AttachEngine3D
  Height = 10
  Placement = pos=(-36.2,-2,12) rot=(0,1,0;1.5708rad)
  Radius = 2
FEATURE [Part::Fillet] Fillet035
  Base = -> Cylinder003
  Edges = 1 edges r=1.8: [Edge3]
FEATURE [Part::Fillet] Fillet036
  Base = -> Fillet035
  Edges = 1 edges r=1.8: [Edge2]
  Placement = pos=(-12.8,0,0) rot=(0,0,1;0rad)
FEATURE [Part::Cylinder] Cylinder004
  Angle = 360
  AttacherType = Attacher::AttachEngine3D
  Height = 10
  Placement = pos=(-36.2,-2,12) rot=(0,1,0;1.5708rad)
  Radius = 2
FEATURE [Part::Fillet] Fillet038
  Base = -> Cylinder004
  Edges = 1 edges r=1.8: [Edge3]
FEATURE [Part::Fillet] Fillet037
  Base = -> Fillet038
  Edges = 1 edges r=1.8: [Edge2]
  Placement = pos=(-6.4,0,0) rot=(0,0,1;0rad)
FEATURE [Sketcher::SketchObject] Sketch048
  FullyConstrained = true
  sketch-geometry (4):
    g0: LineSegment StartX=-5.1 StartY=-34.18 StartZ=0 EndX=5.1 EndY=-34.18 EndZ=0
    g1: LineSegment StartX=-5.1 StartY=-3.93167e-07 StartZ=0 EndX=-5.1 EndY=-34.18 EndZ=0
    g2: LineSegment StartX=5.1 StartY=-34.18 StartZ=0 EndX=5.1 EndY=-3.93167e-07 EndZ=0
    g3: LineSegment StartX=-5.1 StartY=-3.93167e-07 StartZ=0 EndX=5.1 EndY=-3.93167e-07 EndZ=0
  constraints (10):
    c: Horizontal(g0)
    c: Block(g0)
    c: Coincident(g1,g0)
    c: Vertical(g1)
    c: Coincident(g2,g0)
    c: Vertical(g2)
    c: Coincident(g3,g1)
    c: Coincident(g3,g2)
    c: Horizontal(g3)
    c: Block(g3)
FEATURE [Part::Extrusion] Extrude044
  Base = -> Sketch048
  Dir = (0,0,1)
  DirMode = 2
  FaceMakerClass = Part::FaceMakerBullseye
  LengthFwd = 6.2
  LengthRev = 0
  Solid = true
  Symmetric = false
FEATURE [Part::Fillet] Fillet039
  Base = -> Extrude044
  Edges = 1 edges r=3.09: [Edge7]
FEATURE [Part::Fillet] Fillet040
  Base = -> Fillet039
  Edges = 1 edges r=3.09: [Edge8]
FEATURE [Part::Fillet] Fillet041
  Base = -> Fillet040
  Edges = 1 edges r=3.09: [Edge17]
FEATURE [Part::Fillet] Fillet042  label="removeFromMainToMakeUSBCableHole"
  Base = -> Fillet041
  Edges = 1 edges r=3.09: [Edge10]
  Placement = pos=(-111.4,30,10.9) rot=(0,1,0;1.5708rad)
FEATURE [Part::Cylinder] Cylinder
  Angle = 360
  AttacherType = Attacher::AttachEngine3D
  Height = 17.6
  Placement = pos=(-116.86,-14.05,2.4) rot=(0,0,1;0rad)
  Radius = 8.4
FEATURE [Part::Box] Box080  label="Cube080"
  AttacherType = Attacher::AttachEngine3D
  Height = 20
  Length = 6
  Placement = pos=(-120.65,-16.05,2.4) rot=(0,0,-1;0.349066rad)
  Width = 13.85
FEATURE [Part::Cylinder] Cylinder005
  Angle = 360
  AttacherType = Attacher::AttachEngine3D
  Height = 20
  Placement = pos=(-116.86,-14.05,30) rot=(0,0,1;0rad)
  Radius = 11.06
FEATURE [Part::Box] Box081  label="Cube081"
  AttacherType = Attacher::AttachEngine3D
  Height = 20
  Length = 10
  Placement = pos=(-115.9,-3.3,30) rot=(0,0,-1;0.314159rad)
  Width = 10
FEATURE [App::MeasureDistance] Distance001  label="Distance: 2.40 mm"
  Distance = 2.4
  P1 = (-129.5,-19.3,2.4)
  P2 = (-129.5,-19.3,0)
FEATURE [Part::MultiFuse] Fusion047
  Shapes = -> [Box080,Cylinder]
FEATURE [Part::Cylinder] Cylinder006
  Angle = 360
  AttacherType = Attacher::AttachEngine3D
  Height = 10
  Placement = pos=(-112,-13.1,17) rot=(0,1,0;1.5708rad)
  Radius = 4.4
FEATURE [Part::MultiFuse] Fusion048  label="removeFromMainToCreateHoleForUSBCablePillar"
  Shapes = -> [Fusion047,Cylinder006]
FEATURE [Part::Extrusion] Extrude046
  Base = -> Sketch047
  Dir = (0,0,1)
  DirMode = 2
  FaceMakerClass = Part::FaceMakerBullseye
  LengthFwd = 8
  LengthRev = 0
  Solid = true
  Symmetric = false
FEATURE [App::MeasureDistance] Distance002  label="Distance: 12.20 mm"
  Distance = 12.2
  P1 = (32.7,-36,8)
  P2 = (20.5,-36,8)
FEATURE [Part::Fillet] Fillet
  Base = -> Extrude046
  Edges = 1 edges r=3.9: [Edge12]
FEATURE [Part::Fillet] Fillet048
  Base = -> Fillet
  Edges = 1 edges r=3.9: [Edge8]
FEATURE [Part::Fillet] Fillet049
  Base = -> Fillet048
  Edges = 1 edges r=3.9: [Edge17]
FEATURE [Part::Fillet] Fillet050
  Base = -> Fillet049
  Edges = 1 edges r=3.9: [Edge11]
  Placement = pos=(-55,0,8.3) rot=(1,0,0;0.191986rad)
FEATURE [Part::MultiFuse] Fusion049
  Shapes = -> [Fillet031,Fillet036,Fillet037]
FEATURE [Part::Cut] Cut027
  Base = -> Cylinder005
  Placement = pos=(0,0,-30) rot=(0,0,1;0rad)
  Tool = -> Box081
FEATURE [Sketcher::SketchObject] Sketch049
  FullyConstrained = true
  sketch-geometry (4):
    g0: LineSegment StartX=-5.1 StartY=-34.18 StartZ=0 EndX=5.1 EndY=-34.18 EndZ=0
    g1: LineSegment StartX=-5.1 StartY=-3.93167e-07 StartZ=0 EndX=-5.1 EndY=-34.18 EndZ=0
    g2: LineSegment StartX=5.1 StartY=-34.18 StartZ=0 EndX=5.1 EndY=-3.93167e-07 EndZ=0
    g3: LineSegment StartX=-5.1 StartY=-3.93167e-07 StartZ=0 EndX=5.1 EndY=-3.93167e-07 EndZ=0
  constraints (10):
    c: Horizontal(g0)
    c: Block(g0)
    c: Coincident(g1,g0)
    c: Vertical(g1)
    c: Coincident(g2,g0)
    c: Vertical(g2)
    c: Coincident(g3,g1)
    c: Coincident(g3,g2)
    c: Horizontal(g3)
    c: Block(g3)
FEATURE [Part::Extrusion] Extrude047
  Base = -> Sketch049
  Dir = (0,0,1)
  DirMode = 2
  FaceMakerClass = Part::FaceMakerBullseye
  LengthFwd = 6.2
  LengthRev = 0
  Solid = true
  Symmetric = false
FEATURE [Part::Fillet] Fillet054
  Base = -> Extrude047
  Edges = 1 edges r=3.09: [Edge7]
FEATURE [Part::Fillet] Fillet051
  Base = -> Fillet054
  Edges = 1 edges r=3.09: [Edge8]
FEATURE [Part::Fillet] Fillet052
  Base = -> Fillet051
  Edges = 1 edges r=3.09: [Edge17]
FEATURE [Part::Fillet] Fillet053  label="removeFromMainToMakeUSBCableHole001"
  Base = -> Fillet052
  Edges = 1 edges r=3.09: [Edge10]
  Placement = pos=(-111.4,30,14.9) rot=(0,1,0;1.5708rad)
FEATURE [Sketcher::SketchObject] Sketch050
  FullyConstrained = true
  sketch-geometry (4):
    g0: LineSegment StartX=-5.1 StartY=-34.18 StartZ=0 EndX=5.1 EndY=-34.18 EndZ=0
    g1: LineSegment StartX=-5.1 StartY=-3.93167e-07 StartZ=0 EndX=-5.1 EndY=-34.18 EndZ=0
    g2: LineSegment StartX=5.1 StartY=-34.18 StartZ=0 EndX=5.1 EndY=-3.93167e-07 EndZ=0
    g3: LineSegment StartX=-5.1 StartY=-3.93167e-07 StartZ=0 EndX=5.1 EndY=-3.93167e-07 EndZ=0
  constraints (10):
    c: Horizontal(g0)
    c: Block(g0)
    c: Coincident(g1,g0)
    c: Vertical(g1)
    c: Coincident(g2,g0)
    c: Vertical(g2)
    c: Coincident(g3,g1)
    c: Coincident(g3,g2)
    c: Horizontal(g3)
    c: Block(g3)
FEATURE [Part::Extrusion] Extrude048
  Base = -> Sketch050
  Dir = (0,0,1)
  DirMode = 2
  FaceMakerClass = Part::FaceMakerBullseye
  LengthFwd = 6.2
  LengthRev = 0
  Solid = true
  Symmetric = false
FEATURE [Part::Fillet] Fillet058
  Base = -> Extrude048
  Edges = 1 edges r=3.09: [Edge7]
FEATURE [Part::Fillet] Fillet056
  Base = -> Fillet058
  Edges = 1 edges r=3.09: [Edge8]
FEATURE [Part::Fillet] Fillet055
  Base = -> Fillet056
  Edges = 1 edges r=3.09: [Edge17]
FEATURE [Part::Fillet] Fillet057  label="removeFromMainToMakeUSBCableHole002"
  Base = -> Fillet055
  Edges = 1 edges r=3.09: [Edge10]
  Placement = pos=(-111.4,30,18.4) rot=(0,1,0;1.5708rad)
FEATURE [Part::MultiFuse] Fusion050  label="removeFusion050"
  Shapes = -> [Fillet057,Fillet053,Fillet042]
FEATURE [Part::Box] Box082  label="Cube082"
  AttacherType = Attacher::AttachEngine3D
  Height = 3
  Length = 3
  Placement = pos=(-20,-23.5,17) rot=(0,0,1;0rad)
  Width = 23
FEATURE [Part::Box] Box083  label="Cube083"
  AttacherType = Attacher::AttachEngine3D
  Height = 3
  Length = 3
  Placement = pos=(-40,-23.5,17) rot=(0,0,1;0rad)
  Width = 23
FEATURE [Part::Box] Box086  label="Cube086"
  AttacherType = Attacher::AttachEngine3D
  Height = 8
  Length = 28
  Placement = pos=(-132,-26,0) rot=(0,0,1;0rad)
  Width = 23
FEATURE [Part::Box] Box087  label="Cube087"
  AttacherType = Attacher::AttachEngine3D
  Height = 8
  Length = 12
  Placement = pos=(-98,-26,0) rot=(0,0,1;0rad)
  Width = 23
FEATURE [Part::Box] Box088  label="Cube088"
  AttacherType = Attacher::AttachEngine3D
  Height = 8
  Length = 12
  Placement = pos=(-108,-10,0) rot=(0,0,1;0rad)
  Width = 8
FEATURE [Part::MultiFuse] Fusion051  label="extraStrengthFusion051"
  Shapes = -> [Box087,Box088,Box086]
FEATURE [Part::Fillet] Fillet059
  Base = -> Fusion051
  Edges = 1 edges r=4: [Edge8]
FEATURE [Part::MultiFuse] Fusion052  label="main"
  Shapes = -> [Box083,Box082,Cut017,Extrude001,Fillet059,Revolve]
FEATURE [Part::Cut] Cut028
  Base = -> Fusion052
  Tool = -> Fusion050
FEATURE [Part::Fillet] Fillet060
  Base = -> Cut028
  Edges = 1 edges r=2: [Edge287]
FEATURE [Part::Cut] Cut029
  Base = -> Fillet060
  Tool = -> Fillet050
FEATURE [Part::Cut] Cut030
  Base = -> Cut029
  Tool = -> Fusion049
FEATURE [Part::Cut] Cut031  label="mainCut031"
  Base = -> Cut030
  Tool = -> Fusion037
FEATURE [App::MeasureDistance] Distance003  label="Distance: 69.20 mm"
  Distance = 69.2
  P1 = (-2.5,-29.6975,8.49911)
  P2 = (-71.7,-29.6975,8.49911)
FEATURE [App::MeasureDistance] Distance004  label="Distance: 10.00 mm"
  Distance = 10
  P1 = (-56.7,-29.6975,8.49911)
  P2 = (-46.7,-29.6975,8.49911)
FEATURE [Sketcher::SketchObject] Sketch051
  FullyConstrained = true
  MapMode = 4
  Placement = pos=(0,0,0) rot=(0.57735,0.57735,0.57735;2.0944rad)
  sketch-geometry (14):
    g0: LineSegment StartX=6.08745 StartY=-4.11588 StartZ=0 EndX=6.08745 EndY=-2.11589 EndZ=0
    g1: LineSegment StartX=8.08745 StartY=1.38411 StartZ=0 EndX=8.08745 EndY=-1.11589 EndZ=0
    g2: ArcOfCircle CenterX=7.08745 CenterY=-1.11589 CenterZ=0 NormalX=0 NormalY=0 NormalZ=1 AngleXU=0 Radius=1 StartAngle=4.71239 EndAngle=6.28319
    g3: LineSegment StartX=6.08745 StartY=-2.11589 StartZ=0 EndX=7.08745 EndY=-2.11589 EndZ=0
    g4: LineSegment StartX=6.08745 StartY=-4.11588 StartZ=0 EndX=7.08745 EndY=-4.11588 EndZ=0
    g5: ArcOfCircle CenterX=7.08745 CenterY=-1.11589 CenterZ=0 NormalX=0 NormalY=0 NormalZ=1 AngleXU=0 Radius=3 StartAngle=4.71239 EndAngle=6.28319
    g6: ArcOfCircle CenterX=7.08745 CenterY=1.38411 CenterZ=0 NormalX=0 NormalY=0 NormalZ=1 AngleXU=0 Radius=1 StartAngle=5.35e-14 EndAngle=1.5708
    g7: LineSegment StartX=10.0875 StartY=-1.11588 StartZ=0 EndX=10.0875 EndY=1.38411 EndZ=0
    g8: ArcOfCircle CenterX=7.08745 CenterY=1.38411 CenterZ=0 NormalX=0 NormalY=0 NormalZ=1 AngleXU=0 Radius=3 StartAngle=3.57e-14 EndAngle=1.5708
    g9: ArcOfCircle CenterX=4.58745 CenterY=1.38412 CenterZ=0 NormalX=0 NormalY=0 NormalZ=1 AngleXU=0 Radius=1 StartAngle=1.57081 EndAngle=3.14159
    g10: LineSegment StartX=4.58744 StartY=2.38411 StartZ=0 EndX=7.08745 EndY=2.38411 EndZ=0
    g11: LineSegment StartX=4.58745 StartY=4.38411 StartZ=0 EndX=7.08745 EndY=4.38411 EndZ=0
    g12: ArcOfCircle CenterX=4.58745 CenterY=5.38411 CenterZ=0 NormalX=0 NormalY=0 NormalZ=1 AngleXU=0 Radius=1 StartAngle=3.14159 EndAngle=4.71239
    g13: LineSegment StartX=3.58745 StartY=5.38411 StartZ=0 EndX=3.58745 EndY=1.38411 EndZ=0
  constraints (33):
    c: Vertical(g0)
    c: Block(g0)
    c: Block(g1)
    c: Coincident(g2,g1)
    c: Coincident(g3,g0)
    c: Coincident(g3,g2)
    c: Horizontal(g3)
    c: Block(g2)
    c: Coincident(g4,g0)
    c: Horizontal(g4)
    c: Coincident(g5,g2)
    c: Block(g5)
    c: Block(g4)
    c: Coincident(g6,g1)
    c: Block(g6)
    c: Coincident(g7,g5)
    c: Vertical(g7)
    c: Coincident(g8,g6)
    c: Block(g8)
    c: Block(g7)
    c: Coincident(g10,g9)
    c: Coincident(g10,g6)
    c: Horizontal(g10)
    c: Block(g10)
    c: Block(g9)
    c: Coincident(g11,g8)
    c: Horizontal(g11)
    c: Block(g12)
    c: Block(g11)
    c: Coincident(g13,g12)
    c: Coincident(g13,g9)
    c: Vertical(g13)
    c: Tangent(g13,g9)
FEATURE [Part::Extrusion] Extrude049
  Base = -> Sketch051
  Dir = (1,0,0)
  DirMode = 2
  FaceMakerClass = Part::FaceMakerBullseye
  LengthFwd = 10
  LengthRev = 0
  Placement = pos=(-34.55,-22.61,4.115) rot=(0,0,1;3.14159rad)
  Solid = true
  Symmetric = false
